# Revit family: LDA_BIM_CARGADOR_EQ241977
name_source: partatom
category: Equipos especializados
units: mm (PartAtom-declared; Revit-internal decimal feet)

## family parameters
Compartido = No
Corte con vacíos al cargar = No
Cota de conector redondo = Diámetro de uso
Punto de cálculo de habitación = No
Se basa en plano de trabajo = No
Siempre vertical = Sí
Tipo de pieza = Normal

## types (1)
- SON 24V 12A MS150 RACK
    Alarm outputs = 1.5mm² plug-in
    Altitude = Over 2000 m, the max operating temperature decreases of 5ºC every 1000 m
    Auxiliary outputs = 2.5mm² plug-in
    Battery output = 50mm²
    Battery temperature compensation = The output battery voltage is compensated by the battery temperature (sensor placed as close as possible). If the sensor is broken or disconnected or has short circuit, the battery voltage isn't compensated
    Class = class I
    Descripción = Cargador de baterias 3600W
    Dimensions = The housing is a 19’’, 2U rack with connections on the back side. The deepth without connectors is 344mm, and 399 with connectors.
    Efficiency at 20% of load = 82%
    Efficiency at full load = 87%
    Elevación por defecto = 0 mm  [stored 0 ft]
    Fabricante = SLAT
    Frequency = 47 à 63Hz
    Hygrometry = Storage: relative humidity from 10 to 95% // Operating: relative humidity from 20 to 95% with no condensation
    IP (front side) = IP 30
    Internal impedance threshold of the battery fault = 20mΩ +/-10% if jumper in '50' position // 130mΩ +/-10% if jumper in '75' position
    Lifetime = 200000h with external ambient temperature of 25ºC, nominal mains voltage, 48h full charging per year and for the rest of the time: 25% of load
    Low battery voltage protection = Low voltage disconnection threshold: 21.6V+/-3%
    Main outputs = 16mm² plug-in and lockable
    Mains = 2.5mm² plug-in (IEC320) and lockable
    Mains voltage = 230V+/-15% (195 à 264V)
    Maximum battery capacity = 225Ah
    Maximum power for all outputs = 3600 W
    Maximum power for all outputs drawn from the battery = 2400W if jumper is on '50' position // 3600W if jumper is on '75' position
    Maximum power per amplifier outputs = 960 W
    Maximum power per controller outputs = 120 W
    Minimun battery capacity = 65Ah if jumper is on '50' position // 86Ah if jumper is on '75' position
    Modelo = SON 24V 12A MS150 RACK
    Neutral and earthing systems = TT, TN, IT
    Nominal output rectifier current = 12A
    Number of amplifier outputs = 6
    Number of controller outputs = 3
    Own rectifier consumption = 430mA
    Peak to peak HF residual voltage (20MHz-50Ω) = <4% of floating voltage
    Power at full load = 380W
    RMS LF residual voltage = <0.2% of floating voltage
    Static and dynamic regulation characteristic = <5% of floating for mains voltage and output load (from 10 to 90%)
    Temperature = Storage: -25 to +85 ºC // Operating: -5 to +45ºC
    Temperature sensor = 1.5mm² plug-in
    Weight = 5.4 kg

note: [stored X ft] marks values corroborated as IEEE doubles in the binary element streams (Revit-internal decimal feet)

## geometry (parser evidence)
native form markers: Sweep x2
no freeform markers — native parametric forms only
